# Revit family: Reece_Back Rest_Wolfen_Back Rest
name_source: partatom
category: Plumbing Fixtures
revit_build: Autodesk Revit 2018 (Build: 20190510_1515(x64)
units: mm (PartAtom-declared; Revit-internal decimal feet)

## family parameters
Always vertical = Yes
Cut with Voids When Loaded = Yes
Part Type = Normal
Room Calculation Point = No
Round Connector Dimension = Use Diameter
Shared = No
Work Plane-Based = Yes

## types (1)
- White_Stainless Steel
    Default Elevation = 0 mm  [stored 0 ft]
    Description = Wolfen Back Rest with Fixed Arms White and Stainless Steel
    Disclaimer = THIS FILE IS THE PROPERTY OF THE REECE GROUP. IT MAY NOT BE REPRODUCED, REVERSE-ENGINEERED OR MODIFIED. ANY REPUBLICATION, TRANSMISSION OR DISTRIBUTION FOR THE PURPOSE OF COMMERCIALLY EXPLOITING THE FILES IS PROHIBITED.
    Keynote = Product #9507171, Reece_Back Rest_Wolfen_Back Rest - White_Stainless Steel
    Manufacturer = Wolfen
    Model = -
    Reece_Accessory_Projection = 315 mm
    Reece_Detail_Disclaimer = THIS FILE IS THE PROPERTY OF THE REECE GROUP. IT MAY NOT BE REPRODUCED, REVERSE-ENGINEERED OR MODIFIED. ANY REPUBLICATION, TRANSMISSION OR DISTRIBUTION FOR THE PURPOSE OF COMMERCIALLY EXPLOITING THE FILES IS PROHIBITED.
    Reece_Material_Main = Reece_Plastic_White
    Reece_Material_Secondary = Reece_Brass_Brushed Stainless Steel
    Reece_Overall_Height = 180 mm  [stored 0.590551 ft]
    Reece_Overall_Length = 330 mm
    Reece_Overall_Width = 400 mm  [stored 1.31234 ft]
    Reece_Product_Brand = Wolfen
    Reece_Product_Description = Wolfen Back Rest with Fixed Arms White and Stainless Steel
    Reece_Product_Mount = Wall Mounted
    Reece_Product_Number = 9507171
    Reece_Product_Sub Brand = -
    Reece_Product_Type = Back Rest
    Reece_Product_Web Page = https://www.reece.com.au
    Type Comments = Back Rest
    URL = https://www.reece.com.au

note: [stored X ft] marks values corroborated as IEEE doubles in the binary element streams (Revit-internal decimal feet)

## geometry (parser evidence)
native form markers: Sweep x2
no freeform markers — native parametric forms only
